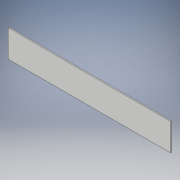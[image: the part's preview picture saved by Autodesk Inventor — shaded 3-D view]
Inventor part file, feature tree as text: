
AUTODESK INVENTOR PART (.ipt)
format: ipt  version: 2017 (Build 210142000, 142)  size: 89,088 bytes
history: native  units: in
note: dims shown in document units (in); Inventor stores cm internally (conversion verified against a paired STEP export)
features: extrude x1, sketch x1
ambient origin geometry x8: Origin, YZ Plane, XZ Plane, XY Plane, X Axis, Y Axis, Z Axis, Center Point
bodies: Solid1 (feature_tree)
feature tree (2):
  extrude  "Extrusion1"  Depth=12.0in
  sketch  "Sketch1"  dims[d0=72.0in d1=12.0in d2=0.5in d3=0.0in]
